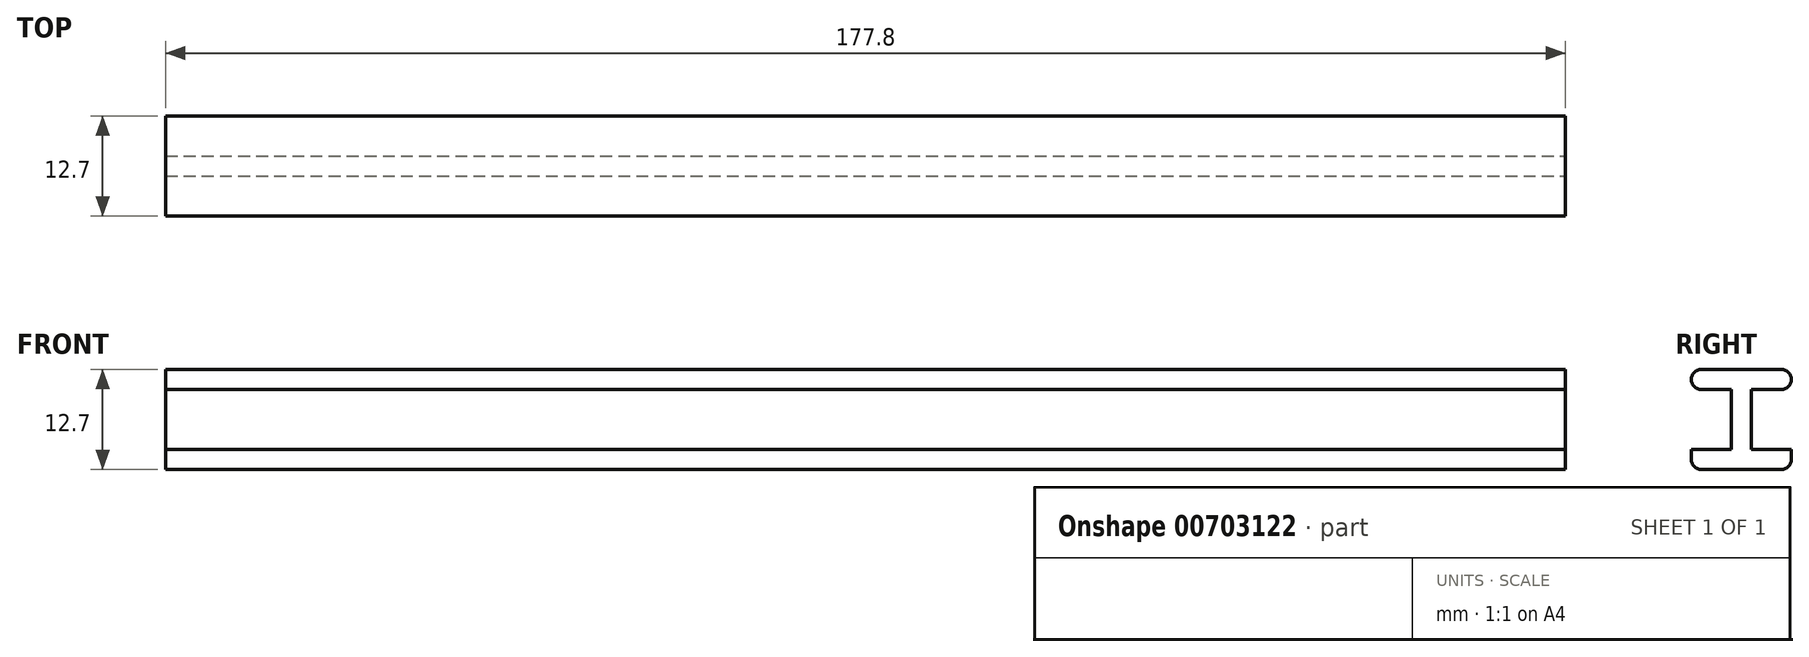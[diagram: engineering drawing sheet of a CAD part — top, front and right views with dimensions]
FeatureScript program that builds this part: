
annotation { "Feature Type Name" : "Feature", "Feature Type Description" : "" }
export const myFeature = defineFeature(function(context is Context, id is Id, definition is map)
    precondition{}
    {
        {
            var Q0;
            Q0=qCreatedBy(makeId("Top.planeOp"),FACE);
            var sketch = newSketch(context, id + "F0", { "sketchPlane" : qUnion([Q0])});
            skLineSegment(sketch, "E0.bottom", {"start": v(88.9, -6.35) * mm, "end": v(-88.9, -6.35) * mm});
            skLineSegment(sketch, "E0.top", {"start": v(88.9, 6.35) * mm, "end": v(-88.9, 6.35) * mm});
            skLineSegment(sketch, "E0.left", {"start": v(88.9, -6.35) * mm, "end": v(88.9, 6.35) * mm});
            skLineSegment(sketch, "E0.right", {"start": v(-88.9, -6.35) * mm, "end": v(-88.9, 6.35) * mm});
            skPoint(sketch, "E0.middle", {"position": v(0, 0) * mm});
            skSolve(sketch);
        }
        {
            var Q0;
            Q0=makeQuery(id+"F0.imprint","IMPRINT",FACE,{"disambiguationData":[TD([[makeQuery(id+"F0.imprint","IMPRINT",EDGE,{"derivedFrom":sQuery(id+"F0.wireOp",EDGE,"E0.bottom")}),-1.0]])]});
            extrude(context, id + "F1", {"entities" : qUnion([Q0]), "depth" : 12.7 * mm, "offsetDistance" : 25.4 * mm});
        }
        {
            var Q0;
            Q0=makeQuery(id+"F1.opExtrude","CAP_EDGE",EDGE,{"disambiguationData":[OSD([sQuery(id+"F0.wireOp",EDGE,"E0.top")])],"isStart":false});
            var Q1;
            Q1=makeQuery(id+"F1.opExtrude","CAP_EDGE",EDGE,{"disambiguationData":[OSD([sQuery(id+"F0.wireOp",EDGE,"E0.bottom")])],"isStart":false});
            var Q2;
            Q2=makeQuery(id+"F1.opExtrude","CAP_EDGE",EDGE,{"disambiguationData":[OSD([sQuery(id+"F0.wireOp",EDGE,"E0.top")])],"isStart":true});
            var Q3;
            Q3=makeQuery(id+"F1.opExtrude","CAP_EDGE",EDGE,{"disambiguationData":[OSD([sQuery(id+"F0.wireOp",EDGE,"E0.bottom")])],"isStart":true});
            fillet(context, id + "F2", {"entities" : qUnion([Q0, Q1, Q2, Q3]), "radius" : 1.27 * mm, "tangentPropagation" : true, "allowEdgeOverflow" : false});
        }
        {
            var Q0;
            Q0=makeQuery(id+"F1.opExtrude","SWEPT_FACE",FACE,{"disambiguationData":[OSD([sQuery(id+"F0.wireOp",EDGE,"E0.left")])]});
            var sketch = newSketch(context, id + "F3", { "sketchPlane" : qUnion([Q0])});
            skLineSegment(sketch, "E1.bottom", {"start": v(-6.35, 10.16) * mm, "end": v(-1.27, 10.16) * mm});
            skLineSegment(sketch, "E1.top", {"start": v(-6.35, 2.54) * mm, "end": v(-1.27, 2.54) * mm});
            skLineSegment(sketch, "E1.left", {"start": v(-6.35, 10.16) * mm, "end": v(-6.35, 2.54) * mm});
            skLineSegment(sketch, "E1.right", {"start": v(-1.27, 10.16) * mm, "end": v(-1.27, 2.54) * mm});
            skLineSegment(sketch, "E2.bottom", {"start": v(6.35, 10.16) * mm, "end": v(1.27, 10.16) * mm});
            skLineSegment(sketch, "E2.top", {"start": v(6.35, 2.54) * mm, "end": v(1.27, 2.54) * mm});
            skLineSegment(sketch, "E2.left", {"start": v(6.35, 10.16) * mm, "end": v(6.35, 2.54) * mm});
            skLineSegment(sketch, "E2.right", {"start": v(1.27, 10.16) * mm, "end": v(1.27, 2.54) * mm});
            skSolve(sketch);
        }
        {
            var Q0;
            Q0=makeQuery(id+"F3.imprint","IMPRINT",FACE,{"disambiguationData":[TD([[makeQuery(id+"F3.imprint","IMPRINT",EDGE,{"derivedFrom":sQuery(id+"F3.wireOp",EDGE,"E1.bottom")}),-1.0]])]});
            var Q1;
            Q1=makeQuery(id+"F3.imprint","IMPRINT",FACE,{"disambiguationData":[TD([[makeQuery(id+"F3.imprint","IMPRINT",EDGE,{"derivedFrom":sQuery(id+"F3.wireOp",EDGE,"E2.bottom")}),1.0]])]});
            extrude(context, id + "F4", {"entities" : qUnion([Q0, Q1]), "operationType" : NewBodyOperationType.REMOVE, "oppositeDirection" : true, "depth" : 177.8 * mm, "offsetDistance" : 25.4 * mm});
        }
        {
            var Q0;
            Q0=makeQuery(id+"F4.boolean.opBoolean","COPY",EDGE,{"derivedFrom":makeQuery(id+"F4.opExtrude","SWEPT_EDGE",EDGE,{"disambiguationData":[OSD([sQuery(id+"F0.wireOp",EDGE,"E0.bottom"),sQuery(id+"F0.wireOp",EDGE,"E0.left"),sQuery(id+"F3.wireOp",EDGE,"E1.bottom"),sQuery(id+"F3.wireOp",EDGE,"E1.left")])]})});
            var Q1;
            Q1=makeQuery(id+"F4.boolean.opBoolean","COPY",EDGE,{"derivedFrom":makeQuery(id+"F4.opExtrude","SWEPT_EDGE",EDGE,{"disambiguationData":[OSD([sQuery(id+"F0.wireOp",EDGE,"E0.bottom"),sQuery(id+"F0.wireOp",EDGE,"E0.left"),sQuery(id+"F3.wireOp",EDGE,"E1.top"),sQuery(id+"F3.wireOp",EDGE,"E1.left")])]})});
            var Q2;
            Q2=makeQuery(id+"F4.boolean.opBoolean","COPY",EDGE,{"derivedFrom":makeQuery(id+"F4.opExtrude","SWEPT_EDGE",EDGE,{"disambiguationData":[OSD([sQuery(id+"F0.wireOp",EDGE,"E0.top"),sQuery(id+"F0.wireOp",EDGE,"E0.left"),sQuery(id+"F3.wireOp",EDGE,"E2.top"),sQuery(id+"F3.wireOp",EDGE,"E2.left")])]})});
            var Q3;
            Q3=makeQuery(id+"F4.boolean.opBoolean","COPY",EDGE,{"derivedFrom":makeQuery(id+"F4.opExtrude","SWEPT_EDGE",EDGE,{"disambiguationData":[OSD([sQuery(id+"F0.wireOp",EDGE,"E0.top"),sQuery(id+"F0.wireOp",EDGE,"E0.left"),sQuery(id+"F3.wireOp",EDGE,"E2.bottom"),sQuery(id+"F3.wireOp",EDGE,"E2.left")])]})});
            fillet(context, id + "F5", {"entities" : qUnion([Q0, Q1, Q2, Q3]), "radius" : 1.27 * mm, "tangentPropagation" : true, "allowEdgeOverflow" : false});
        }
    });
